# Revit family: QF_ELECTROLUXPROFESSIONAL_602355_ESKTH42L
name_source: partatom
category: Specialty Equipment
units: mm (PartAtom-declared; Revit-internal decimal feet)

## family parameters
Always vertical = Yes
Cut with Voids When Loaded = No
Enable Cutting in Views = No
Maintain Annotation Orientation = No
Part Type = Normal
Room Calculation Point = No
Round Connector Dimension = Use Diameter
Shared = No
Work Plane-Based = No

## types (1)
- QF_ELECTROLUXPROFESSIONAL_602355_ESKTH42L
    Accessory = No
    Cycle = 50 Hz
    Default Elevation = 0 mm  [stored 0 ft]
    Depth Actual = 840 mm
    Description = SPIRAL DOUGH KNEADER, 42LT REMOVABLE BOWL, TILTING HEAD, 2 SPEED, 380-415V/3/50HZ
    Gas KW = 0
    HP = 4 HP
    Height Actual = 800 mm
    Item Number = 602355
    Length Actual = 480 mm
    Manufacturer = Electrolux Professional
    Model = ESKTH42L
    Phase = 3
    Show Logo = Yes
    URL = http://www.electroluxprofessional.com
    URL Manufacturer = http://www.electroluxprofessional.com
    Volts = 380 V
    Watts = 0 W
    Weight = 112.00 kg

note: [stored X ft] marks values corroborated as IEEE doubles in the binary element streams (Revit-internal decimal feet)

## geometry (parser evidence)
native form markers: Sweep x10
no freeform markers — native parametric forms only
